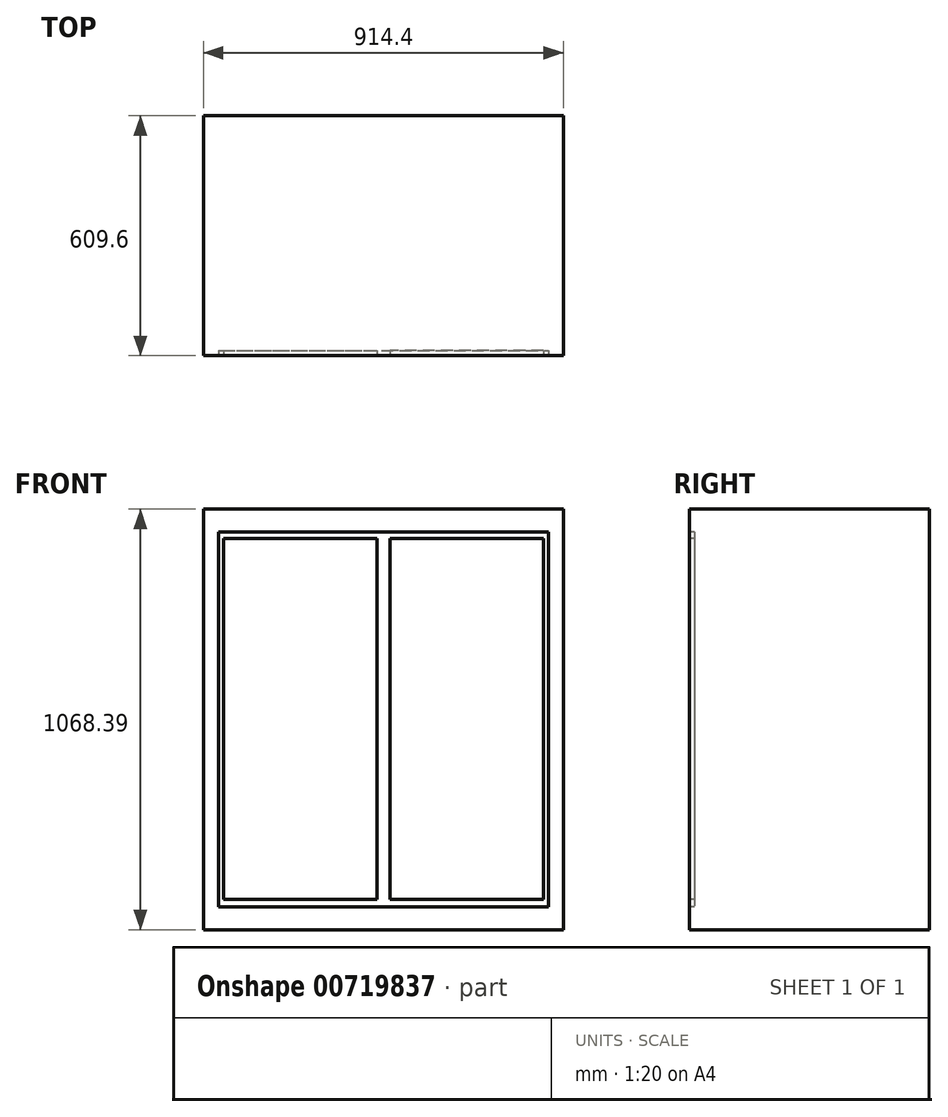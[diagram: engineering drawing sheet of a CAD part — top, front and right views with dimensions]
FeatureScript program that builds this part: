
annotation { "Feature Type Name" : "Feature", "Feature Type Description" : "" }
export const myFeature = defineFeature(function(context is Context, id is Id, definition is map)
    precondition{}
    {
        {
            var Q0;
            Q0=qCreatedBy(makeId("Front.planeOp"),FACE);
            var sketch = newSketch(context, id + "F0", { "sketchPlane" : qUnion([Q0])});
            skLineSegment(sketch, "E0.bottom", {"start": v(-457.2, 1068.39) * mm, "end": v(457.2, 1068.39) * mm});
            skLineSegment(sketch, "E0.top", {"start": v(-457.2, 0) * mm, "end": v(457.2, 0) * mm});
            skLineSegment(sketch, "E0.left", {"start": v(-457.2, 1068.39) * mm, "end": v(-457.2, 0) * mm});
            skLineSegment(sketch, "E0.right", {"start": v(457.2, 1068.39) * mm, "end": v(457.2, 0) * mm});
            skPoint(sketch, "E1", {"position": v(0, 0) * mm});
            skSolve(sketch);
        }
        {
            var Q0;
            Q0=makeQuery(id+"F0.imprint","IMPRINT",FACE,{"disambiguationData":[TD([[makeQuery(id+"F0.imprint","IMPRINT",EDGE,{"derivedFrom":sQuery(id+"F0.wireOp",EDGE,"E0.bottom")}),-1.0]])]});
            extrude(context, id + "F1", {"entities" : qUnion([Q0]), "endBound" : BoundingType.SYMMETRIC, "depth" : 609.6 * mm, "offsetDistance" : 25.4 * mm});
        }
        {
            var Q0;
            Q0=makeQuery(id+"F1.opExtrude","CAP_FACE",FACE,{"disambiguationData":[OSD([sQuery(id+"F0.wireOp",EDGE,"E0.bottom"),sQuery(id+"F0.wireOp",EDGE,"E0.top"),sQuery(id+"F0.wireOp",EDGE,"E0.left"),sQuery(id+"F0.wireOp",EDGE,"E0.right")])],"isStart":false});
            var sketch = newSketch(context, id + "F2", { "sketchPlane" : qUnion([Q0])});
            skPoint(sketch, "E2", {"position": v(0, 534.2) * mm});
            skPoint(sketch, "E3.orphan", {"position": v(-457.2, 1068.39) * mm});
            skPoint(sketch, "E4.end.orphan", {"position": v(457.2, 0) * mm});
            skSolve(sketch);
        }
        {
            var Q0;
            Q0=makeQuery(id+"F2.imprint","IMPRINT",FACE,{"disambiguationData":[TD([[makeQuery(id+"F2.imprint","IMPRINT",EDGE,{"derivedFrom":makeQuery(id+"F1.opExtrude","CAP_EDGE",EDGE,{"disambiguationData":[OSD([sQuery(id+"F0.wireOp",EDGE,"E0.bottom")])],"isStart":false})}),-1.0]])]});
            var sketch = newSketch(context, id + "F3", { "sketchPlane" : qUnion([Q0])});
            skLineSegment(sketch, "E5.bottom", {"start": v(-419.1, 1010.44) * mm, "end": v(0, 1010.44) * mm});
            skLineSegment(sketch, "E5.top", {"start": v(-419.1, 57.94) * mm, "end": v(0, 57.94) * mm});
            skLineSegment(sketch, "E5.left", {"start": v(-419.1, 1010.44) * mm, "end": v(-419.1, 57.94) * mm});
            skLineSegment(sketch, "E5.right", {"start": v(0, 1010.44) * mm, "end": v(0, 57.94) * mm});
            skLineSegment(sketch, "E6.bottom", {"start": v(0, 1010.44) * mm, "end": v(419.1, 1010.44) * mm});
            skLineSegment(sketch, "E6.top", {"start": v(0, 57.94) * mm, "end": v(419.1, 57.94) * mm});
            skLineSegment(sketch, "E6.right", {"start": v(419.1, 1010.44) * mm, "end": v(419.1, 57.94) * mm});
            skPoint(sketch, "E7", {"position": v(0, 534.2) * mm});
            skLineSegment(sketch, "E8.bottom", {"start": v(-406.41, 994.57) * mm, "end": v(-16.25, 994.57) * mm});
            skLineSegment(sketch, "E8.top", {"start": v(-406.41, 76.97) * mm, "end": v(-16.25, 76.97) * mm});
            skLineSegment(sketch, "E8.left", {"start": v(-406.41, 994.57) * mm, "end": v(-406.41, 76.97) * mm});
            skLineSegment(sketch, "E8.right", {"start": v(-16.25, 994.57) * mm, "end": v(-16.25, 76.97) * mm});
            skLineSegment(sketch, "E9.MirrorCS", {"start": v(16.25, 994.57) * mm, "end": v(16.25, 76.97) * mm});
            skLineSegment(sketch, "E10.MirrorCS", {"start": v(406.41, 994.57) * mm, "end": v(16.25, 994.57) * mm});
            skLineSegment(sketch, "E11.MirrorCS", {"start": v(406.41, 994.57) * mm, "end": v(406.41, 76.97) * mm});
            skLineSegment(sketch, "E12.MirrorCS", {"start": v(406.41, 76.97) * mm, "end": v(16.25, 76.97) * mm});
            skSolve(sketch);
        }
        {
            var Q0;
            Q0=sQuery(id+"F3.wireOp",EDGE,"E10.MirrorCS");
            var Q1;
            Q1=sQuery(id+"F3.wireOp",EDGE,"E6.bottom");
            var Q2;
            Q2=sQuery(id+"F3.wireOp",EDGE,"E6.right");
            var Q3;
            Q3=sQuery(id+"F3.wireOp",EDGE,"E11.MirrorCS");
            var Q4;
            Q4=sQuery(id+"F3.wireOp",EDGE,"E12.MirrorCS");
            var Q5;
            Q5=sQuery(id+"F3.wireOp",EDGE,"E6.top");
            var Q6;
            Q6=sQuery(id+"F3.wireOp",EDGE,"E5.right");
            var Q7;
            Q7=sQuery(id+"F3.wireOp",EDGE,"E9.MirrorCS");
            extrude(context, id + "F4", {"bodyType" : ToolBodyType.SURFACE, "surfaceEntities" : qUnion([Q0, Q1, Q2, Q3, Q4, Q5, Q6, Q7]), "depth" : 0.64 * mm, "offsetDistance" : 25.4 * mm});
        }
        {
            var Q0;
            Q0=qSketchRegion(id+"F3",true);
            extrude(context, id + "F5", {"entities" : qUnion([Q0]), "operationType" : NewBodyOperationType.REMOVE, "oppositeDirection" : true, "depth" : 12.7 * mm, "offsetDistance" : 25.4 * mm});
        }
    });
